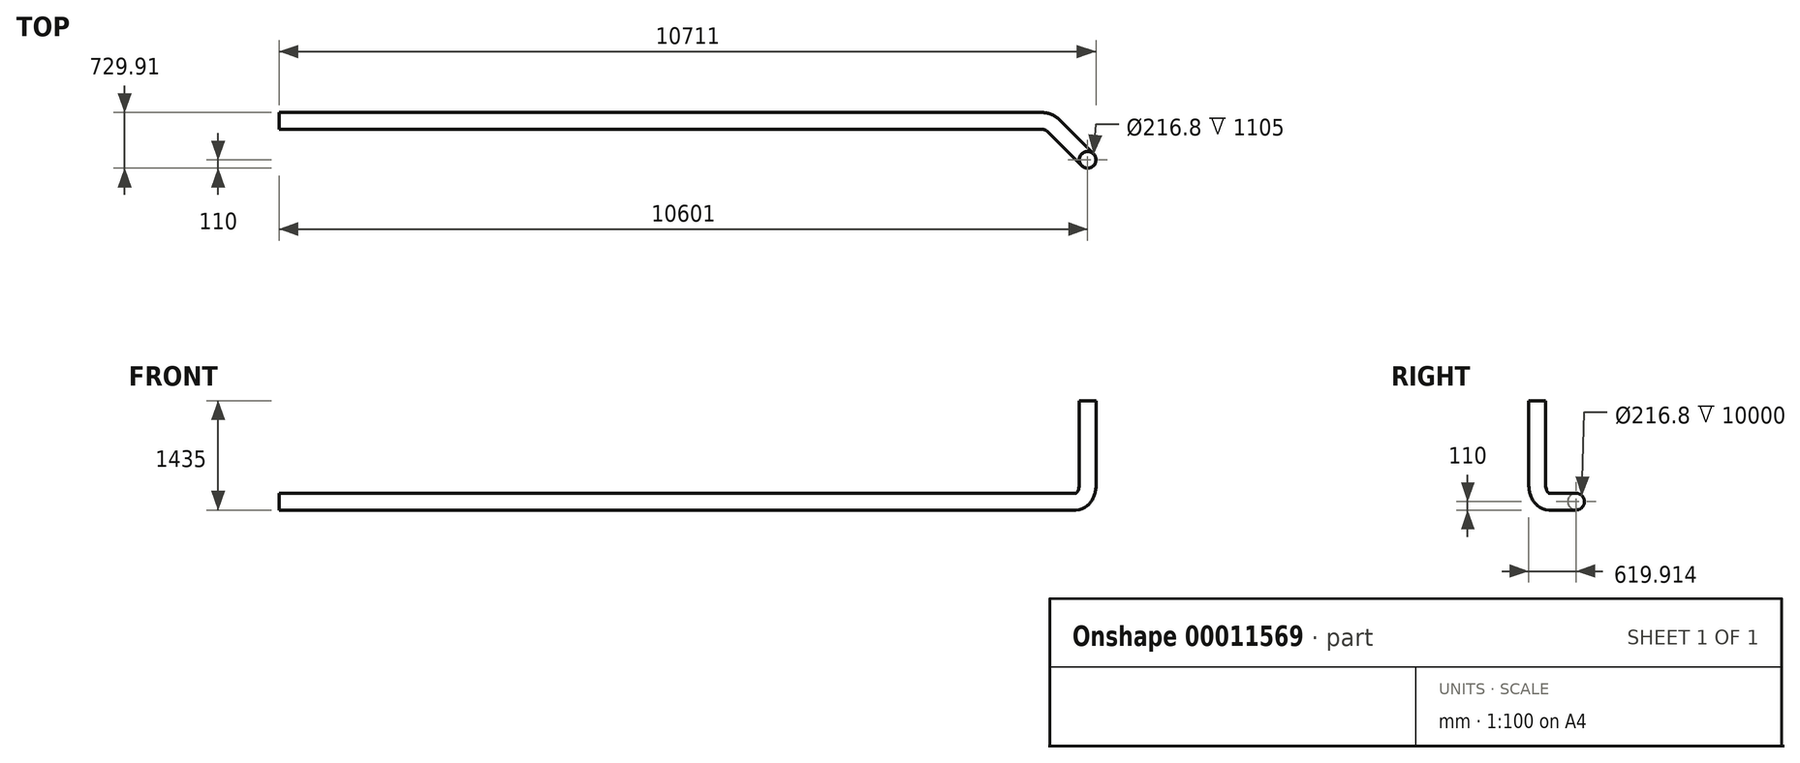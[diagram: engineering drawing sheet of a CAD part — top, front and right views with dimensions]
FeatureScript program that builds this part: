
annotation { "Feature Type Name" : "Feature", "Feature Type Description" : "" }
export const myFeature = defineFeature(function(context is Context, id is Id, definition is map)
    precondition{}
    {
        {
            var Q0;
            Q0=qCreatedBy(makeId("Front.planeOp"),FACE);
            var Q1;
            Q1=qCreatedBy(makeId("Right.planeOp"),FACE);
            cPlane(context, id + "F0", {"entities" : qUnion([Q0, Q1]), "cplaneType" : CPlaneType.MID_PLANE, "offset" : 150 * mm, "width" : 150 * mm, "height" : 150 * mm});
        }
        {
            var Q0;
            Q0=qCreatedBy(makeId("Top.planeOp"),FACE);
            cPlane(context, id + "F1", {"entities" : qUnion([Q0]), "cplaneType" : CPlaneType.OFFSET, "offset" : 1325 * mm, "oppositeDirection" : true, "width" : 150 * mm, "height" : 150 * mm});
        }
        {
            var Q0;
            Q0=qCreatedBy(id+"F0.planeOp",FACE);
            var sketch = newSketch(context, id + "F2", { "sketchPlane" : qUnion([Q0])});
            skLineSegment(sketch, "E0", {"start": v(0, 0) * mm, "end": v(0, -1105) * mm});
            skPoint(sketch, "E1.visualSharp", {"position": v(0, -245) * mm});
            skArc(sketch, "E1.filletArc", {"start": v(-220, -1325) * mm, "mid": v(-64.44, -1260.56) * mm, "end": v(0, -1105) * mm});
            skLineSegment(sketch, "E2", {"start": v(-220, -1325) * mm, "end": v(-505, -1325) * mm});
            skSolve(sketch);
        }
        {
            var Q0;
            Q0=qCreatedBy(id+"F1.planeOp",FACE);
            var sketch = newSketch(context, id + "F3", { "sketchPlane" : qUnion([Q0])});
            skLineSegment(sketch, "E3", {"start": v(-601.04, 509.91) * mm, "end": v(-10601.04, 509.91) * mm});
            skLineSegment(sketch, "E4", {"start": v(-445.48, 445.48) * mm, "end": v(-357.09, 357.09) * mm});
            skPoint(sketch, "E5.visualSharp", {"position": v(-509.91, 509.91) * mm});
            skArc(sketch, "E5.filletArc", {"start": v(-445.48, 445.48) * mm, "mid": v(-516.85, 493.17) * mm, "end": v(-601.04, 509.91) * mm});
            skSolve(sketch);
        }
        {
            var Q0;
            Q0=qCreatedBy(makeId("Top.planeOp"),FACE);
            var sketch = newSketch(context, id + "F4", { "sketchPlane" : qUnion([Q0])});
            skCircle(sketch, "E6", {"center": v(0, 0) * mm, "radius": 110 * mm});
            skSolve(sketch);
        }
        {
            var Q0;
            Q0=qSketchRegion(id+"F4",true);
            var Q1;
            Q1=qBodyType(qCreatedBy(id+"F2",EDGE),BodyType.WIRE);
            var Q2;
            Q2=qBodyType(qCreatedBy(id+"F3",EDGE),BodyType.WIRE);
            sweep(context, id + "F5", {"profiles" : qUnion([Q0]), "path" : qUnion([Q1, Q2])});
        }
        {
            var Q0;
            Q0=makeQuery(id+"F5.opSweep","CAP_FACE",FACE,{"disambiguationData":[OSD([sQuery(id+"F2.wireOp",VERTEX,"E0.start"),sQuery(id+"F4.wireOp",EDGE,"E6")])],"isStart":true});
            var Q1;
            Q1=makeQuery(id+"F5.opSweep","CAP_FACE",FACE,{"disambiguationData":[OSD([sQuery(id+"F3.wireOp",VERTEX,"E3.end"),sQuery(id+"F4.wireOp",EDGE,"E6")])],"isStart":false});
            shell(context, id + "F6", {"entities" : qUnion([Q0, Q1]), "thickness" : 1.6 * mm});
        }
    });
